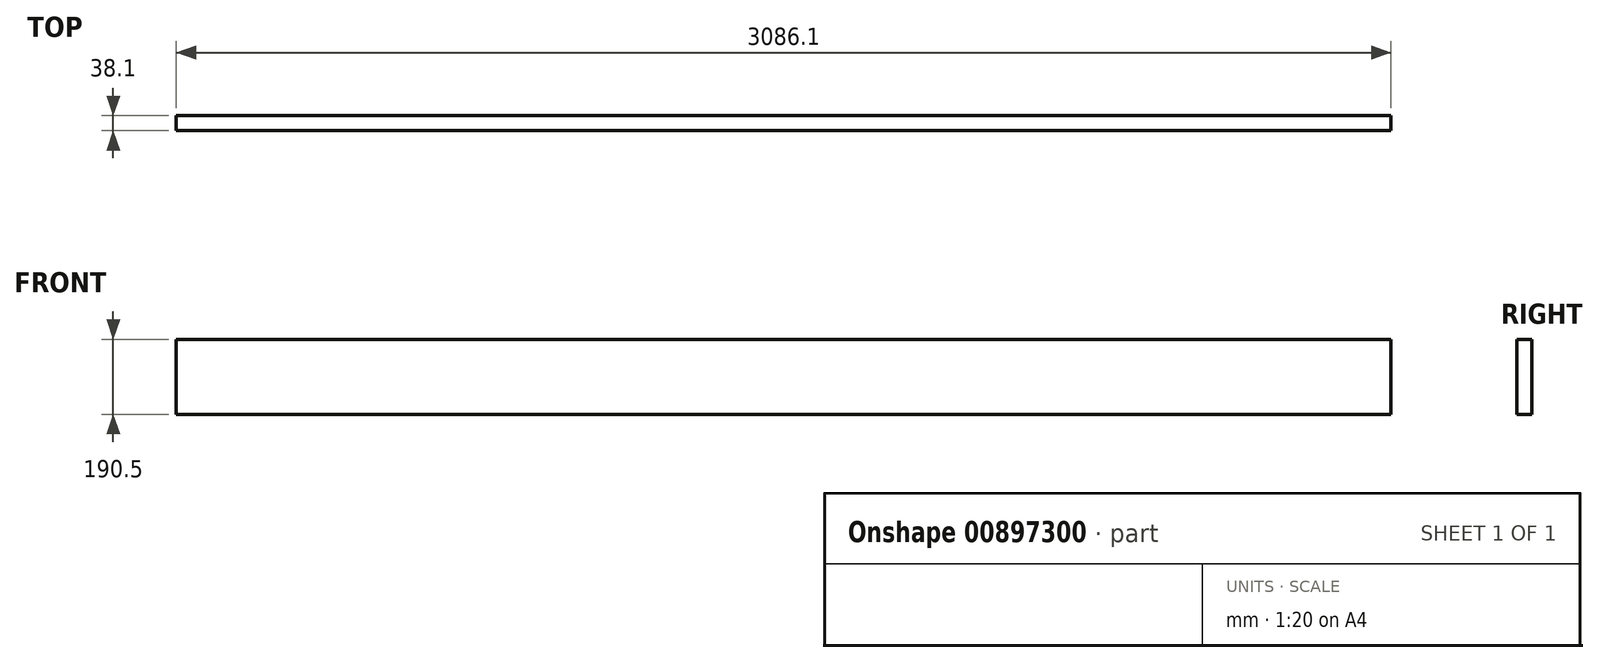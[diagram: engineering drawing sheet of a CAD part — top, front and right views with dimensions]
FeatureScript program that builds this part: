
annotation { "Feature Type Name" : "Feature", "Feature Type Description" : "" }
export const myFeature = defineFeature(function(context is Context, id is Id, definition is map)
    precondition{}
    {
        {
            var Q0;
            Q0=qCreatedBy(makeId("Front.planeOp"),FACE);
            var sketch = newSketch(context, id + "F0", { "sketchPlane" : qUnion([Q0])});
            skLineSegment(sketch, "E0.bottom", {"start": v(-3029.13, 175.66) * mm, "end": v(56.97, 175.66) * mm});
            skLineSegment(sketch, "E0.top", {"start": v(-3029.13, -14.84) * mm, "end": v(56.97, -14.84) * mm});
            skLineSegment(sketch, "E0.left", {"start": v(-3029.13, 175.66) * mm, "end": v(-3029.13, -14.84) * mm});
            skLineSegment(sketch, "E0.right", {"start": v(56.97, 175.66) * mm, "end": v(56.97, -14.84) * mm});
            skSolve(sketch);
        }
        {
            var Q0;
            Q0=makeQuery(id+"F0.imprint","IMPRINT",FACE,{"disambiguationData":[TD([[makeQuery(id+"F0.imprint","IMPRINT",EDGE,{"derivedFrom":sQuery(id+"F0.wireOp",EDGE,"E0.bottom")}),-1.0]])]});
            extrude(context, id + "F1", {"entities" : qUnion([Q0]), "depth" : 38.1 * mm, "offsetDistance" : 25.4 * mm});
        }
    });
